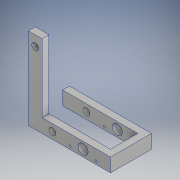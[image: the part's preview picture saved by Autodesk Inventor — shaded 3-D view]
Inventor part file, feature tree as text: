
AUTODESK INVENTOR PART (.ipt)
format: ipt  version: 2019 (Build 230136000, 136)  size: 169,984 bytes
history: native  units: in
note: dims shown in document units (in); Inventor stores cm internally (conversion verified against a paired STEP export)
features: sketch x6, hole x4, extrude x2, projected_geometry x2
ambient origin geometry x8: Origin, YZ Plane, XZ Plane, XY Plane, X Axis, Y Axis, Z Axis, Center Point
bodies: Solid1 (feature_tree)
feature tree (14):
  extrude  "Extrusion1"  Depth=0.5in
  hole  "Hole1"  [1 undecoded]
  hole  "Hole2"  [1 undecoded]
  hole  "Hole3"  [1 undecoded]
  extrude  "Extrusion2"  Depth=2.0in
  hole  "Hole6"  [1 undecoded]
  sketch  "3D Sketch1"
  sketch  "Sketch2"  dims[d1=0.5in d4=0.5in]
  sketch  "Sketch3"  dims[d6=1.0in d7=0.0in d8=1.75in]
  projected_geometry  "Projected Loop1"
  sketch  "Sketch4"  dims[d9=1.0in d10=0.5in]
  projected_geometry  "Projected Loop2"
  sketch  "Sketch5"  dims[d11=0.5in d12=0.75in d13=0.375in d14=0.25in d15=0.5635in d16=1.0in d17=0.8108in d18=1.0in]
  sketch  "Sketch8"  dims[d19=0.5in d20=2.0in d21=0.728in d22=0.75in d23=0.375in d24=0.25in d25=0.5635in d26=1.0in d27=0.8108in d28=1.89in d29=0.276in d30=0.276in d31=0.945in d32=0.146in d33=0.75in d34=0.375in d35=0.25in d36=0.5635in d37=1.0in d38=0.8108in d39=0.5in d41=5.0in d42=0.0in d63=0.5in d64=6.0in d65=6.0in d66=2.0in d67=1.0in d68=0.0in d69=0.0in d70=0.75in d71=1.0in d72=0.5in d73=0.5in d74=0.75in d75=0.375in d76=0.25in d77=0.5635in d78=1.0in d79=0.8108in]
note: 4 required parameter values undecoded (feature->parameter linkage not recoverable at this tier; creation-order binding heuristic only, values carry confidence <= 0.55)
